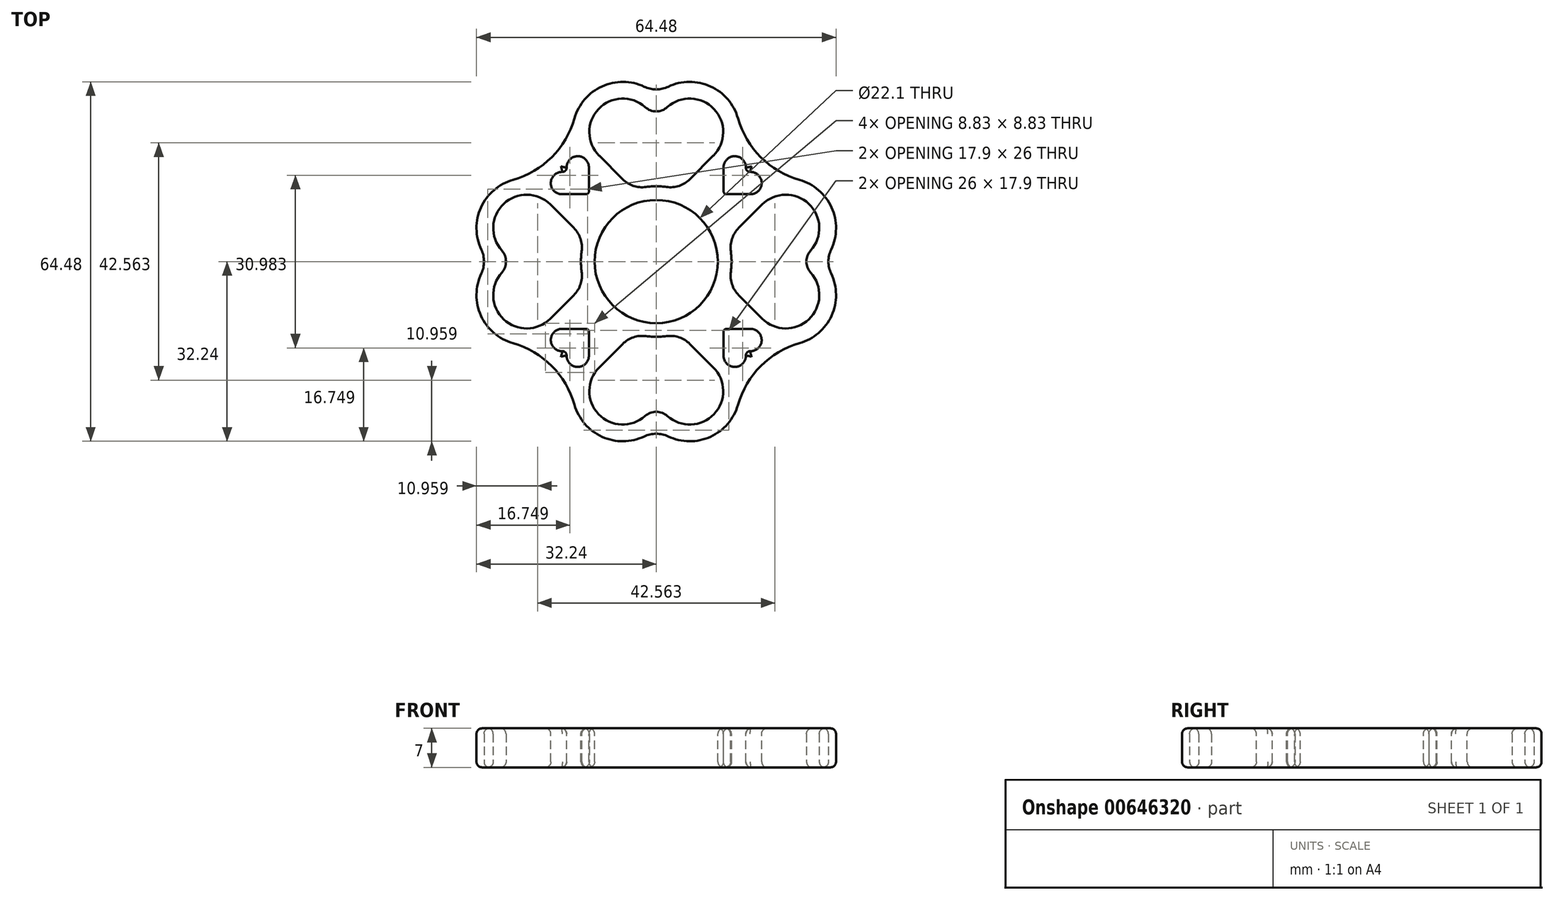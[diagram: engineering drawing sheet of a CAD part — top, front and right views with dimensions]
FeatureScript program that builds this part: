
annotation { "Feature Type Name" : "Feature", "Feature Type Description" : "" }
export const myFeature = defineFeature(function(context is Context, id is Id, definition is map)
    precondition{}
    {
        {
            var Q0;
            Q0=qCreatedBy(makeId("Top.planeOp"),FACE);
            var sketch = newSketch(context, id + "F0", { "sketchPlane" : qUnion([Q0])});
            skLineSegment(sketch, "E0", {"start": v(0, 0) * mm, "end": v(0, 35.78) * mm, "construction": true});
            skArc(sketch, "E1", {"start": v(-2, 27.71) * mm, "mid": v(-10.36, 27.36) * mm, "end": v(-10.24, 19) * mm});
            skLineSegment(sketch, "E2", {"start": v(-10.24, 19) * mm, "end": v(-1.41, 10.17) * mm});
            skArc(sketch, "E3", {"start": v(10.24, 19) * mm, "mid": v(10.36, 27.36) * mm, "end": v(2, 27.71) * mm});
            skLineSegment(sketch, "E4", {"start": v(10.24, 19) * mm, "end": v(1.41, 10.17) * mm});
            skPoint(sketch, "E5.visualSharp", {"position": v(0, 23.24) * mm});
            skArc(sketch, "E5.filletArc", {"start": v(-2, 27.71) * mm, "mid": v(0, 26.95) * mm, "end": v(2, 27.71) * mm});
            skPoint(sketch, "E6.visualSharp", {"position": v(0, 8.75) * mm});
            skArc(sketch, "E6.filletArc", {"start": v(-1.41, 10.17) * mm, "mid": v(0, 9.58) * mm, "end": v(1.41, 10.17) * mm});
            skArc(sketch, "E7.1", {"start": v(-2.14, 31.37) * mm, "mid": v(-9.72, 31.43) * mm, "end": v(-14.66, 25.7) * mm});
            skArc(sketch, "E7.4", {"start": v(14.66, 25.7) * mm, "mid": v(9.72, 31.43) * mm, "end": v(2.14, 31.37) * mm});
            skArc(sketch, "E8.filletArc", {"start": v(-2.14, 31.37) * mm, "mid": v(0, 30.89) * mm, "end": v(2.14, 31.37) * mm});
            skPoint(sketch, "E9.1.0", {"position": v(-8.75, 0) * mm});
            skArc(sketch, "E9.1.1", {"start": v(-25.7, 14.66) * mm, "mid": v(-31.43, 9.72) * mm, "end": v(-31.37, 2.14) * mm});
            skArc(sketch, "E9.1.4", {"start": v(-31.37, -2.14) * mm, "mid": v(-31.43, -9.72) * mm, "end": v(-25.7, -14.66) * mm});
            skArc(sketch, "E9.1.6", {"start": v(-27.71, -2) * mm, "mid": v(-26.95, 0) * mm, "end": v(-27.71, 2) * mm});
            skLineSegment(sketch, "E9.1.7", {"start": v(-19, 10.24) * mm, "end": v(-10.17, 1.41) * mm});
            skArc(sketch, "E9.1.8", {"start": v(-19, 10.24) * mm, "mid": v(-27.36, 10.36) * mm, "end": v(-27.71, 2) * mm});
            skLineSegment(sketch, "E9.1.9", {"start": v(-19, -10.24) * mm, "end": v(-10.17, -1.41) * mm});
            skArc(sketch, "E9.1.10", {"start": v(-27.71, -2) * mm, "mid": v(-27.36, -10.36) * mm, "end": v(-19, -10.24) * mm});
            skLineSegment(sketch, "E9.1.11", {"start": v(0, 0) * mm, "end": v(-35.78, 0) * mm, "construction": true});
            skPoint(sketch, "E9.1.12", {"position": v(-23.24, 0) * mm});
            skPoint(sketch, "E9.1.13", {"position": v(-29.95, 0) * mm});
            skArc(sketch, "E9.1.14", {"start": v(-10.17, -1.41) * mm, "mid": v(-9.58, 0) * mm, "end": v(-10.17, 1.41) * mm});
            skArc(sketch, "E9.1.15", {"start": v(-31.37, -2.14) * mm, "mid": v(-30.89, 0) * mm, "end": v(-31.37, 2.14) * mm});
            skPoint(sketch, "E9.2.0", {"position": v(0, -8.75) * mm});
            skArc(sketch, "E9.2.1", {"start": v(-14.66, -25.7) * mm, "mid": v(-9.72, -31.43) * mm, "end": v(-2.14, -31.37) * mm});
            skArc(sketch, "E9.2.4", {"start": v(2.14, -31.37) * mm, "mid": v(9.72, -31.43) * mm, "end": v(14.66, -25.7) * mm});
            skArc(sketch, "E9.2.6", {"start": v(2, -27.71) * mm, "mid": v(0, -26.95) * mm, "end": v(-2, -27.71) * mm});
            skLineSegment(sketch, "E9.2.7", {"start": v(-10.24, -19) * mm, "end": v(-1.41, -10.17) * mm});
            skArc(sketch, "E9.2.8", {"start": v(-10.24, -19) * mm, "mid": v(-10.36, -27.36) * mm, "end": v(-2, -27.71) * mm});
            skLineSegment(sketch, "E9.2.9", {"start": v(10.24, -19) * mm, "end": v(1.41, -10.17) * mm});
            skArc(sketch, "E9.2.10", {"start": v(2, -27.71) * mm, "mid": v(10.36, -27.36) * mm, "end": v(10.24, -19) * mm});
            skLineSegment(sketch, "E9.2.11", {"start": v(0, 0) * mm, "end": v(0, -35.78) * mm, "construction": true});
            skPoint(sketch, "E9.2.12", {"position": v(0, -23.24) * mm});
            skPoint(sketch, "E9.2.13", {"position": v(0, -29.95) * mm});
            skArc(sketch, "E9.2.14", {"start": v(1.41, -10.17) * mm, "mid": v(0, -9.58) * mm, "end": v(-1.41, -10.17) * mm});
            skArc(sketch, "E9.2.15", {"start": v(2.14, -31.37) * mm, "mid": v(0, -30.89) * mm, "end": v(-2.14, -31.37) * mm});
            skPoint(sketch, "E9.3.0", {"position": v(8.75, 0) * mm});
            skArc(sketch, "E9.3.1", {"start": v(25.7, -14.66) * mm, "mid": v(31.43, -9.72) * mm, "end": v(31.37, -2.14) * mm});
            skArc(sketch, "E9.3.4", {"start": v(31.37, 2.14) * mm, "mid": v(31.43, 9.72) * mm, "end": v(25.7, 14.66) * mm});
            skArc(sketch, "E9.3.6", {"start": v(27.71, 2) * mm, "mid": v(26.95, 0) * mm, "end": v(27.71, -2) * mm});
            skLineSegment(sketch, "E9.3.7", {"start": v(19, -10.24) * mm, "end": v(10.17, -1.41) * mm});
            skArc(sketch, "E9.3.8", {"start": v(19, -10.24) * mm, "mid": v(27.36, -10.36) * mm, "end": v(27.71, -2) * mm});
            skLineSegment(sketch, "E9.3.9", {"start": v(19, 10.24) * mm, "end": v(10.17, 1.41) * mm});
            skArc(sketch, "E9.3.10", {"start": v(27.71, 2) * mm, "mid": v(27.36, 10.36) * mm, "end": v(19, 10.24) * mm});
            skLineSegment(sketch, "E9.3.11", {"start": v(0, 0) * mm, "end": v(35.78, 0) * mm, "construction": true});
            skPoint(sketch, "E9.3.12", {"position": v(23.24, 0) * mm});
            skPoint(sketch, "E9.3.13", {"position": v(29.95, 0) * mm});
            skArc(sketch, "E9.3.14", {"start": v(10.17, 1.41) * mm, "mid": v(9.58, 0) * mm, "end": v(10.17, -1.41) * mm});
            skArc(sketch, "E9.3.15", {"start": v(31.37, 2.14) * mm, "mid": v(30.89, 0) * mm, "end": v(31.37, -2.14) * mm});
            skPoint(sketch, "E9.center", {"position": v(0, 0) * mm});
            skCircle(sketch, "E10.converted", {"center": v(0, 0) * mm, "radius": 30 * mm, "construction": true});
            skArc(sketch, "E11", {"start": v(-26.26, 14.5) * mm, "mid": v(-18.74, 18.74) * mm, "end": v(-14.5, 26.26) * mm});
            skArc(sketch, "E12", {"start": v(14.5, 26.26) * mm, "mid": v(18.74, 18.74) * mm, "end": v(26.26, 14.5) * mm});
            skArc(sketch, "E13", {"start": v(-14.5, -26.26) * mm, "mid": v(-18.74, -18.74) * mm, "end": v(-26.26, -14.5) * mm});
            skArc(sketch, "E14", {"start": v(26.26, -14.5) * mm, "mid": v(18.74, -18.74) * mm, "end": v(14.5, -26.26) * mm});
            skSolve(sketch);
        }
        {
            var Q0;
            Q0=makeQuery(id+"F0.imprint","IMPRINT",FACE,{"disambiguationData":[TD([[makeQuery(id+"F0.imprint","IMPRINT",EDGE,{"derivedFrom":sQuery(id+"F0.wireOp",EDGE,"E1")}),-1.0]])]});
            extrude(context, id + "F1", {"entities" : qUnion([Q0]), "depth" : 7 * mm, "offsetDistance" : 25 * mm});
        }
        {
            var Q0;
            Q0=makeQuery(id+"F1.opExtrude","CAP_FACE",FACE,{"disambiguationData":[OSD([sQuery(id+"F0.wireOp",EDGE,"E1"),sQuery(id+"F0.wireOp",EDGE,"E2"),sQuery(id+"F0.wireOp",EDGE,"E3"),sQuery(id+"F0.wireOp",EDGE,"E4"),sQuery(id+"F0.wireOp",EDGE,"E5.filletArc"),sQuery(id+"F0.wireOp",EDGE,"E6.filletArc"),sQuery(id+"F0.wireOp",EDGE,"E7.1"),sQuery(id+"F0.wireOp",EDGE,"E7.4"),sQuery(id+"F0.wireOp",EDGE,"E8.filletArc"),sQuery(id+"F0.wireOp",EDGE,"E9.1.1"),sQuery(id+"F0.wireOp",EDGE,"E9.1.4"),sQuery(id+"F0.wireOp",EDGE,"E9.1.6"),sQuery(id+"F0.wireOp",EDGE,"E9.1.7"),sQuery(id+"F0.wireOp",EDGE,"E9.1.8"),sQuery(id+"F0.wireOp",EDGE,"E9.1.9"),sQuery(id+"F0.wireOp",EDGE,"E9.1.10"),sQuery(id+"F0.wireOp",EDGE,"E9.1.14"),sQuery(id+"F0.wireOp",EDGE,"E9.1.15"),sQuery(id+"F0.wireOp",EDGE,"E9.2.1"),sQuery(id+"F0.wireOp",EDGE,"E9.2.4"),sQuery(id+"F0.wireOp",EDGE,"E9.2.6"),sQuery(id+"F0.wireOp",EDGE,"E9.2.7"),sQuery(id+"F0.wireOp",EDGE,"E9.2.8"),sQuery(id+"F0.wireOp",EDGE,"E9.2.9"),sQuery(id+"F0.wireOp",EDGE,"E9.2.10"),sQuery(id+"F0.wireOp",EDGE,"E9.2.14"),sQuery(id+"F0.wireOp",EDGE,"E9.2.15"),sQuery(id+"F0.wireOp",EDGE,"E9.3.1"),sQuery(id+"F0.wireOp",EDGE,"E9.3.4"),sQuery(id+"F0.wireOp",EDGE,"E9.3.6"),sQuery(id+"F0.wireOp",EDGE,"E9.3.7"),sQuery(id+"F0.wireOp",EDGE,"E9.3.8"),sQuery(id+"F0.wireOp",EDGE,"E9.3.9"),sQuery(id+"F0.wireOp",EDGE,"E9.3.10"),sQuery(id+"F0.wireOp",EDGE,"E9.3.14"),sQuery(id+"F0.wireOp",EDGE,"E9.3.15"),sQuery(id+"F0.wireOp",EDGE,"E11"),sQuery(id+"F0.wireOp",EDGE,"E12"),sQuery(id+"F0.wireOp",EDGE,"E13"),sQuery(id+"F0.wireOp",EDGE,"E14")])],"isStart":false});
            var sketch = newSketch(context, id + "F2", { "sketchPlane" : qUnion([Q0])});
            skCircle(sketch, "E15", {"center": v(0, 0) * mm, "radius": 13.5 * mm});
            skSolve(sketch);
        }
        {
            var Q0;
            Q0 = qSketchRegion(id + "F2", true);
            extrude(context, id + "F3", {"entities" : qUnion([Q0]), "operationType" : NewBodyOperationType.ADD, "oppositeDirection" : true, "depth" : 7 * mm, "offsetDistance" : 25 * mm});
        }
        {
            var Q0;
            Q0=makeQuery(id+"F3.boolean.opBoolean","MERGE",FACE,{"derivedFrom":[makeQuery(id+"F1.opExtrude","CAP_FACE",FACE,{"disambiguationData":[OSD([sQuery(id+"F0.wireOp",EDGE,"E1"),sQuery(id+"F0.wireOp",EDGE,"E2"),sQuery(id+"F0.wireOp",EDGE,"E3"),sQuery(id+"F0.wireOp",EDGE,"E4"),sQuery(id+"F0.wireOp",EDGE,"E5.filletArc"),sQuery(id+"F0.wireOp",EDGE,"E6.filletArc"),sQuery(id+"F0.wireOp",EDGE,"E7.1"),sQuery(id+"F0.wireOp",EDGE,"E7.4"),sQuery(id+"F0.wireOp",EDGE,"E8.filletArc"),sQuery(id+"F0.wireOp",EDGE,"E9.1.1"),sQuery(id+"F0.wireOp",EDGE,"E9.1.4"),sQuery(id+"F0.wireOp",EDGE,"E9.1.6"),sQuery(id+"F0.wireOp",EDGE,"E9.1.7"),sQuery(id+"F0.wireOp",EDGE,"E9.1.8"),sQuery(id+"F0.wireOp",EDGE,"E9.1.9"),sQuery(id+"F0.wireOp",EDGE,"E9.1.10"),sQuery(id+"F0.wireOp",EDGE,"E9.1.14"),sQuery(id+"F0.wireOp",EDGE,"E9.1.15"),sQuery(id+"F0.wireOp",EDGE,"E9.2.1"),sQuery(id+"F0.wireOp",EDGE,"E9.2.4"),sQuery(id+"F0.wireOp",EDGE,"E9.2.6"),sQuery(id+"F0.wireOp",EDGE,"E9.2.7"),sQuery(id+"F0.wireOp",EDGE,"E9.2.8"),sQuery(id+"F0.wireOp",EDGE,"E9.2.9"),sQuery(id+"F0.wireOp",EDGE,"E9.2.10"),sQuery(id+"F0.wireOp",EDGE,"E9.2.14"),sQuery(id+"F0.wireOp",EDGE,"E9.2.15"),sQuery(id+"F0.wireOp",EDGE,"E9.3.1"),sQuery(id+"F0.wireOp",EDGE,"E9.3.4"),sQuery(id+"F0.wireOp",EDGE,"E9.3.6"),sQuery(id+"F0.wireOp",EDGE,"E9.3.7"),sQuery(id+"F0.wireOp",EDGE,"E9.3.8"),sQuery(id+"F0.wireOp",EDGE,"E9.3.9"),sQuery(id+"F0.wireOp",EDGE,"E9.3.10"),sQuery(id+"F0.wireOp",EDGE,"E9.3.14"),sQuery(id+"F0.wireOp",EDGE,"E9.3.15"),sQuery(id+"F0.wireOp",EDGE,"E11"),sQuery(id+"F0.wireOp",EDGE,"E12"),sQuery(id+"F0.wireOp",EDGE,"E13"),sQuery(id+"F0.wireOp",EDGE,"E14")])],"isStart":false}),makeQuery(id+"F3.opExtrude","CAP_FACE",FACE,{"disambiguationData":[OSD([sQuery(id+"F2.wireOp",EDGE,"iwJjpqlm-qK7G-SQGB-iVIw-FQQKzJX3b7a8"),sQuery(id+"F2.wireOp",EDGE,"E15")])],"isStart":true})]});
            var sketch = newSketch(context, id + "F4", { "sketchPlane" : qUnion([Q0])});
            skCircle(sketch, "E16", {"center": v(0, 0) * mm, "radius": 11.05 * mm});
            skSolve(sketch);
        }
        {
            var Q0;
            Q0 = qSketchRegion(id + "F4", true);
            extrude(context, id + "F5", {"entities" : qUnion([Q0]), "operationType" : NewBodyOperationType.REMOVE, "endBound" : BoundingType.THROUGH_ALL, "oppositeDirection" : true, "depth" : 25 * mm, "offsetDistance" : 25 * mm});
        }
        {
            var Q0;
            Q0=makeQuery(id+"F3.boolean.opBoolean","INTERSECT",EDGE,{"derivedFrom":[makeQuery(id+"F1.opExtrude","SWEPT_FACE",FACE,{"disambiguationData":[OSD([sQuery(id+"F0.wireOp",EDGE,"E2")])]}),makeQuery(id+"F3.opExtrude","SWEPT_FACE",FACE,{"disambiguationData":[OSD([sQuery(id+"F2.wireOp",EDGE,"E15")])]})]});
            var Q1;
            Q1=makeQuery(id+"F3.boolean.opBoolean","INTERSECT",EDGE,{"derivedFrom":[makeQuery(id+"F1.opExtrude","SWEPT_FACE",FACE,{"disambiguationData":[OSD([sQuery(id+"F0.wireOp",EDGE,"E4")])]}),makeQuery(id+"F3.opExtrude","SWEPT_FACE",FACE,{"disambiguationData":[OSD([sQuery(id+"F2.wireOp",EDGE,"E15")])]})]});
            var Q2;
            Q2=makeQuery(id+"F3.boolean.opBoolean","INTERSECT",EDGE,{"derivedFrom":[makeQuery(id+"F1.opExtrude","SWEPT_FACE",FACE,{"disambiguationData":[OSD([sQuery(id+"F0.wireOp",EDGE,"E9.3.7")])]}),makeQuery(id+"F3.opExtrude","SWEPT_FACE",FACE,{"disambiguationData":[OSD([sQuery(id+"F2.wireOp",EDGE,"E15")])]})]});
            var Q3;
            Q3=makeQuery(id+"F3.boolean.opBoolean","INTERSECT",EDGE,{"derivedFrom":[makeQuery(id+"F1.opExtrude","SWEPT_FACE",FACE,{"disambiguationData":[OSD([sQuery(id+"F0.wireOp",EDGE,"E9.3.9")])]}),makeQuery(id+"F3.opExtrude","SWEPT_FACE",FACE,{"disambiguationData":[OSD([sQuery(id+"F2.wireOp",EDGE,"E15")])]})]});
            var Q4;
            Q4=makeQuery(id+"F3.boolean.opBoolean","INTERSECT",EDGE,{"derivedFrom":[makeQuery(id+"F1.opExtrude","SWEPT_FACE",FACE,{"disambiguationData":[OSD([sQuery(id+"F0.wireOp",EDGE,"E9.1.7")])]}),makeQuery(id+"F3.opExtrude","SWEPT_FACE",FACE,{"disambiguationData":[OSD([sQuery(id+"F2.wireOp",EDGE,"E15")])]})]});
            var Q5;
            Q5=makeQuery(id+"F3.boolean.opBoolean","INTERSECT",EDGE,{"derivedFrom":[makeQuery(id+"F1.opExtrude","SWEPT_FACE",FACE,{"disambiguationData":[OSD([sQuery(id+"F0.wireOp",EDGE,"E9.1.9")])]}),makeQuery(id+"F3.opExtrude","SWEPT_FACE",FACE,{"disambiguationData":[OSD([sQuery(id+"F2.wireOp",EDGE,"E15")])]})]});
            var Q6;
            Q6=makeQuery(id+"F3.boolean.opBoolean","INTERSECT",EDGE,{"derivedFrom":[makeQuery(id+"F1.opExtrude","SWEPT_FACE",FACE,{"disambiguationData":[OSD([sQuery(id+"F0.wireOp",EDGE,"E9.2.7")])]}),makeQuery(id+"F3.opExtrude","SWEPT_FACE",FACE,{"disambiguationData":[OSD([sQuery(id+"F2.wireOp",EDGE,"E15")])]})]});
            var Q7;
            Q7=makeQuery(id+"F3.boolean.opBoolean","INTERSECT",EDGE,{"derivedFrom":[makeQuery(id+"F1.opExtrude","SWEPT_FACE",FACE,{"disambiguationData":[OSD([sQuery(id+"F0.wireOp",EDGE,"E9.2.9")])]}),makeQuery(id+"F3.opExtrude","SWEPT_FACE",FACE,{"disambiguationData":[OSD([sQuery(id+"F2.wireOp",EDGE,"E15")])]})]});
            fillet(context, id + "F6", {"entities" : qUnion([Q0, Q1, Q2, Q3, Q4, Q5, Q6, Q7]), "radius" : 5 * mm, "tangentPropagation" : true, "allowEdgeOverflow" : false});
        }
        {
            var Q0;
            Q0=makeQuery(id+"F3.boolean.opBoolean","MERGE",FACE,{"derivedFrom":[makeQuery(id+"F1.opExtrude","CAP_FACE",FACE,{"disambiguationData":[OSD([sQuery(id+"F0.wireOp",EDGE,"E1"),sQuery(id+"F0.wireOp",EDGE,"E2"),sQuery(id+"F0.wireOp",EDGE,"E3"),sQuery(id+"F0.wireOp",EDGE,"E4"),sQuery(id+"F0.wireOp",EDGE,"E5.filletArc"),sQuery(id+"F0.wireOp",EDGE,"E6.filletArc"),sQuery(id+"F0.wireOp",EDGE,"E7.1"),sQuery(id+"F0.wireOp",EDGE,"E7.4"),sQuery(id+"F0.wireOp",EDGE,"E8.filletArc"),sQuery(id+"F0.wireOp",EDGE,"E9.1.1"),sQuery(id+"F0.wireOp",EDGE,"E9.1.4"),sQuery(id+"F0.wireOp",EDGE,"E9.1.6"),sQuery(id+"F0.wireOp",EDGE,"E9.1.7"),sQuery(id+"F0.wireOp",EDGE,"E9.1.8"),sQuery(id+"F0.wireOp",EDGE,"E9.1.9"),sQuery(id+"F0.wireOp",EDGE,"E9.1.10"),sQuery(id+"F0.wireOp",EDGE,"E9.1.14"),sQuery(id+"F0.wireOp",EDGE,"E9.1.15"),sQuery(id+"F0.wireOp",EDGE,"E9.2.1"),sQuery(id+"F0.wireOp",EDGE,"E9.2.4"),sQuery(id+"F0.wireOp",EDGE,"E9.2.6"),sQuery(id+"F0.wireOp",EDGE,"E9.2.7"),sQuery(id+"F0.wireOp",EDGE,"E9.2.8"),sQuery(id+"F0.wireOp",EDGE,"E9.2.9"),sQuery(id+"F0.wireOp",EDGE,"E9.2.10"),sQuery(id+"F0.wireOp",EDGE,"E9.2.14"),sQuery(id+"F0.wireOp",EDGE,"E9.2.15"),sQuery(id+"F0.wireOp",EDGE,"E9.3.1"),sQuery(id+"F0.wireOp",EDGE,"E9.3.4"),sQuery(id+"F0.wireOp",EDGE,"E9.3.6"),sQuery(id+"F0.wireOp",EDGE,"E9.3.7"),sQuery(id+"F0.wireOp",EDGE,"E9.3.8"),sQuery(id+"F0.wireOp",EDGE,"E9.3.9"),sQuery(id+"F0.wireOp",EDGE,"E9.3.10"),sQuery(id+"F0.wireOp",EDGE,"E9.3.14"),sQuery(id+"F0.wireOp",EDGE,"E9.3.15"),sQuery(id+"F0.wireOp",EDGE,"E11"),sQuery(id+"F0.wireOp",EDGE,"E12"),sQuery(id+"F0.wireOp",EDGE,"E13"),sQuery(id+"F0.wireOp",EDGE,"E14")])],"isStart":false}),makeQuery(id+"F3.opExtrude","CAP_FACE",FACE,{"disambiguationData":[OSD([sQuery(id+"F2.wireOp",EDGE,"iwJjpqlm-qK7G-SQGB-iVIw-FQQKzJX3b7a8"),sQuery(id+"F2.wireOp",EDGE,"E15")])],"isStart":true})]});
            var sketch = newSketch(context, id + "F7", { "sketchPlane" : qUnion([Q0])});
            skLineSegment(sketch, "E17", {"start": v(0, 0) * mm, "end": v(-28.28, 28.28) * mm, "construction": true});
            skCircle(sketch, "E18", {"center": v(0, 0) * mm, "radius": 24 * mm, "construction": true});
            skArc(sketch, "E19", {"start": v(-12.08, 16.9) * mm, "mid": v(-14.1, 18.9) * mm, "end": v(-16.08, 16.85) * mm});
            skArc(sketch, "E20", {"start": v(-16.85, 16.08) * mm, "mid": v(-18.9, 14.1) * mm, "end": v(-16.9, 12.08) * mm});
            skLineSegment(sketch, "E21", {"start": v(-16.9, 12.08) * mm, "end": v(-12.58, 12.08) * mm});
            skLineSegment(sketch, "E22", {"start": v(-12.08, 12.58) * mm, "end": v(-12.08, 16.9) * mm});
            skArc(sketch, "E23", {"start": v(-16.85, 16.08) * mm, "mid": v(-16.3, 16.3) * mm, "end": v(-16.08, 16.85) * mm});
            skPoint(sketch, "E24.visualSharp", {"position": v(-12.08, 12.08) * mm});
            skArc(sketch, "E24.filletArc", {"start": v(-12.58, 12.08) * mm, "mid": v(-12.22, 12.22) * mm, "end": v(-12.08, 12.58) * mm});
            skPoint(sketch, "E25.1.0", {"position": v(-12.08, -12.08) * mm});
            skArc(sketch, "E25.1.1", {"start": v(-16.9, -12.08) * mm, "mid": v(-18.9, -14.1) * mm, "end": v(-16.85, -16.08) * mm});
            skLineSegment(sketch, "E25.1.2", {"start": v(-12.58, -12.08) * mm, "end": v(-16.9, -12.08) * mm});
            skArc(sketch, "E25.1.3", {"start": v(-16.08, -16.85) * mm, "mid": v(-14.1, -18.9) * mm, "end": v(-12.08, -16.9) * mm});
            skLineSegment(sketch, "E25.1.4", {"start": v(-12.08, -16.9) * mm, "end": v(-12.08, -12.58) * mm});
            skArc(sketch, "E25.1.5", {"start": v(-16.08, -16.85) * mm, "mid": v(-16.3, -16.3) * mm, "end": v(-16.85, -16.08) * mm});
            skArc(sketch, "E25.1.6", {"start": v(-12.08, -12.58) * mm, "mid": v(-12.22, -12.22) * mm, "end": v(-12.58, -12.08) * mm});
            skPoint(sketch, "E25.2.0", {"position": v(12.08, -12.08) * mm});
            skArc(sketch, "E25.2.1", {"start": v(12.08, -16.9) * mm, "mid": v(14.1, -18.9) * mm, "end": v(16.08, -16.85) * mm});
            skLineSegment(sketch, "E25.2.2", {"start": v(12.08, -12.58) * mm, "end": v(12.08, -16.9) * mm});
            skArc(sketch, "E25.2.3", {"start": v(16.85, -16.08) * mm, "mid": v(18.9, -14.1) * mm, "end": v(16.9, -12.08) * mm});
            skLineSegment(sketch, "E25.2.4", {"start": v(16.9, -12.08) * mm, "end": v(12.58, -12.08) * mm});
            skArc(sketch, "E25.2.5", {"start": v(16.85, -16.08) * mm, "mid": v(16.3, -16.3) * mm, "end": v(16.08, -16.85) * mm});
            skArc(sketch, "E25.2.6", {"start": v(12.58, -12.08) * mm, "mid": v(12.22, -12.22) * mm, "end": v(12.08, -12.58) * mm});
            skPoint(sketch, "E25.3.0", {"position": v(12.08, 12.08) * mm});
            skArc(sketch, "E25.3.1", {"start": v(16.9, 12.08) * mm, "mid": v(18.9, 14.1) * mm, "end": v(16.85, 16.08) * mm});
            skLineSegment(sketch, "E25.3.2", {"start": v(12.58, 12.08) * mm, "end": v(16.9, 12.08) * mm});
            skArc(sketch, "E25.3.3", {"start": v(16.08, 16.85) * mm, "mid": v(14.1, 18.9) * mm, "end": v(12.08, 16.9) * mm});
            skLineSegment(sketch, "E25.3.4", {"start": v(12.08, 16.9) * mm, "end": v(12.08, 12.58) * mm});
            skArc(sketch, "E25.3.5", {"start": v(16.08, 16.85) * mm, "mid": v(16.3, 16.3) * mm, "end": v(16.85, 16.08) * mm});
            skArc(sketch, "E25.3.6", {"start": v(12.08, 12.58) * mm, "mid": v(12.22, 12.22) * mm, "end": v(12.58, 12.08) * mm});
            skSolve(sketch);
        }
        {
            var Q0;
            Q0 = qSketchRegion(id + "F7", true);
            extrude(context, id + "F8", {"entities" : qUnion([Q0]), "operationType" : NewBodyOperationType.REMOVE, "endBound" : BoundingType.THROUGH_ALL, "oppositeDirection" : true, "depth" : 25 * mm, "offsetDistance" : 25 * mm});
        }
        {
            var Q0;
            Q0=makeQuery(id+"F3.boolean.opBoolean","MERGE",FACE,{"derivedFrom":[makeQuery(id+"F1.opExtrude","CAP_FACE",FACE,{"disambiguationData":[OSD([sQuery(id+"F0.wireOp",EDGE,"E1"),sQuery(id+"F0.wireOp",EDGE,"E2"),sQuery(id+"F0.wireOp",EDGE,"E3"),sQuery(id+"F0.wireOp",EDGE,"E4"),sQuery(id+"F0.wireOp",EDGE,"E5.filletArc"),sQuery(id+"F0.wireOp",EDGE,"E6.filletArc"),sQuery(id+"F0.wireOp",EDGE,"E7.1"),sQuery(id+"F0.wireOp",EDGE,"E7.4"),sQuery(id+"F0.wireOp",EDGE,"E8.filletArc"),sQuery(id+"F0.wireOp",EDGE,"E9.1.1"),sQuery(id+"F0.wireOp",EDGE,"E9.1.4"),sQuery(id+"F0.wireOp",EDGE,"E9.1.6"),sQuery(id+"F0.wireOp",EDGE,"E9.1.7"),sQuery(id+"F0.wireOp",EDGE,"E9.1.8"),sQuery(id+"F0.wireOp",EDGE,"E9.1.9"),sQuery(id+"F0.wireOp",EDGE,"E9.1.10"),sQuery(id+"F0.wireOp",EDGE,"E9.1.14"),sQuery(id+"F0.wireOp",EDGE,"E9.1.15"),sQuery(id+"F0.wireOp",EDGE,"E9.2.1"),sQuery(id+"F0.wireOp",EDGE,"E9.2.4"),sQuery(id+"F0.wireOp",EDGE,"E9.2.6"),sQuery(id+"F0.wireOp",EDGE,"E9.2.7"),sQuery(id+"F0.wireOp",EDGE,"E9.2.8"),sQuery(id+"F0.wireOp",EDGE,"E9.2.9"),sQuery(id+"F0.wireOp",EDGE,"E9.2.10"),sQuery(id+"F0.wireOp",EDGE,"E9.2.14"),sQuery(id+"F0.wireOp",EDGE,"E9.2.15"),sQuery(id+"F0.wireOp",EDGE,"E9.3.1"),sQuery(id+"F0.wireOp",EDGE,"E9.3.4"),sQuery(id+"F0.wireOp",EDGE,"E9.3.6"),sQuery(id+"F0.wireOp",EDGE,"E9.3.7"),sQuery(id+"F0.wireOp",EDGE,"E9.3.8"),sQuery(id+"F0.wireOp",EDGE,"E9.3.9"),sQuery(id+"F0.wireOp",EDGE,"E9.3.10"),sQuery(id+"F0.wireOp",EDGE,"E9.3.14"),sQuery(id+"F0.wireOp",EDGE,"E9.3.15"),sQuery(id+"F0.wireOp",EDGE,"E11"),sQuery(id+"F0.wireOp",EDGE,"E12"),sQuery(id+"F0.wireOp",EDGE,"E13"),sQuery(id+"F0.wireOp",EDGE,"E14")])],"isStart":false}),makeQuery(id+"F3.opExtrude","CAP_FACE",FACE,{"disambiguationData":[OSD([sQuery(id+"F2.wireOp",EDGE,"iwJjpqlm-qK7G-SQGB-iVIw-FQQKzJX3b7a8"),sQuery(id+"F2.wireOp",EDGE,"E15")])],"isStart":true})]});
            var Q1;
            Q1=makeQuery(id+"F3.boolean.opBoolean","MERGE",FACE,{"derivedFrom":[makeQuery(id+"F1.opExtrude","CAP_FACE",FACE,{"disambiguationData":[OSD([sQuery(id+"F0.wireOp",EDGE,"E1"),sQuery(id+"F0.wireOp",EDGE,"E2"),sQuery(id+"F0.wireOp",EDGE,"E3"),sQuery(id+"F0.wireOp",EDGE,"E4"),sQuery(id+"F0.wireOp",EDGE,"E5.filletArc"),sQuery(id+"F0.wireOp",EDGE,"E6.filletArc"),sQuery(id+"F0.wireOp",EDGE,"E7.1"),sQuery(id+"F0.wireOp",EDGE,"E7.4"),sQuery(id+"F0.wireOp",EDGE,"E8.filletArc"),sQuery(id+"F0.wireOp",EDGE,"E9.1.1"),sQuery(id+"F0.wireOp",EDGE,"E9.1.4"),sQuery(id+"F0.wireOp",EDGE,"E9.1.6"),sQuery(id+"F0.wireOp",EDGE,"E9.1.7"),sQuery(id+"F0.wireOp",EDGE,"E9.1.8"),sQuery(id+"F0.wireOp",EDGE,"E9.1.9"),sQuery(id+"F0.wireOp",EDGE,"E9.1.10"),sQuery(id+"F0.wireOp",EDGE,"E9.1.14"),sQuery(id+"F0.wireOp",EDGE,"E9.1.15"),sQuery(id+"F0.wireOp",EDGE,"E9.2.1"),sQuery(id+"F0.wireOp",EDGE,"E9.2.4"),sQuery(id+"F0.wireOp",EDGE,"E9.2.6"),sQuery(id+"F0.wireOp",EDGE,"E9.2.7"),sQuery(id+"F0.wireOp",EDGE,"E9.2.8"),sQuery(id+"F0.wireOp",EDGE,"E9.2.9"),sQuery(id+"F0.wireOp",EDGE,"E9.2.10"),sQuery(id+"F0.wireOp",EDGE,"E9.2.14"),sQuery(id+"F0.wireOp",EDGE,"E9.2.15"),sQuery(id+"F0.wireOp",EDGE,"E9.3.1"),sQuery(id+"F0.wireOp",EDGE,"E9.3.4"),sQuery(id+"F0.wireOp",EDGE,"E9.3.6"),sQuery(id+"F0.wireOp",EDGE,"E9.3.7"),sQuery(id+"F0.wireOp",EDGE,"E9.3.8"),sQuery(id+"F0.wireOp",EDGE,"E9.3.9"),sQuery(id+"F0.wireOp",EDGE,"E9.3.10"),sQuery(id+"F0.wireOp",EDGE,"E9.3.14"),sQuery(id+"F0.wireOp",EDGE,"E9.3.15"),sQuery(id+"F0.wireOp",EDGE,"E11"),sQuery(id+"F0.wireOp",EDGE,"E12"),sQuery(id+"F0.wireOp",EDGE,"E13"),sQuery(id+"F0.wireOp",EDGE,"E14")])],"isStart":true}),makeQuery(id+"F3.opExtrude","CAP_FACE",FACE,{"disambiguationData":[OSD([sQuery(id+"F2.wireOp",EDGE,"iwJjpqlm-qK7G-SQGB-iVIw-FQQKzJX3b7a8"),sQuery(id+"F2.wireOp",EDGE,"E15")])],"isStart":false})]});
            fillet(context, id + "F9", {"entities" : qUnion([Q0, Q1]), "radius" : 1 * mm, "tangentPropagation" : true, "allowEdgeOverflow" : false});
        }
    });
